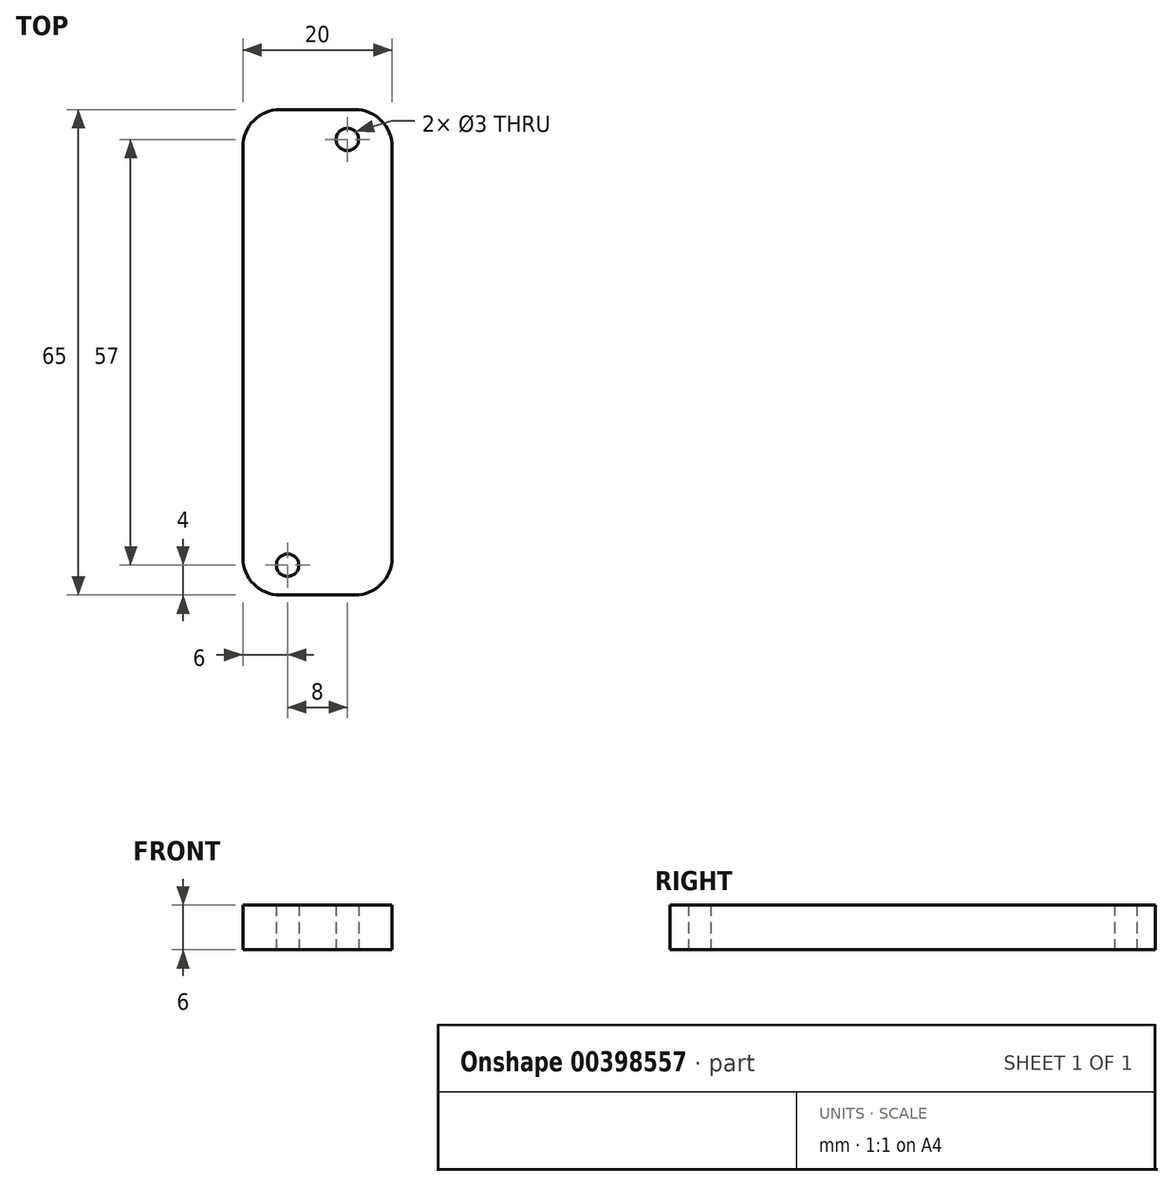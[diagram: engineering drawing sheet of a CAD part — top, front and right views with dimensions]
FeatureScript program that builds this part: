
annotation { "Feature Type Name" : "Feature", "Feature Type Description" : "" }
export const myFeature = defineFeature(function(context is Context, id is Id, definition is map)
    precondition{}
    {
        {
            var Q0;
            Q0=qCreatedBy(makeId("Top.planeOp"),FACE);
            var sketch = newSketch(context, id + "F0", { "sketchPlane" : qUnion([Q0])});
            skLineSegment(sketch, "E0.bottom", {"start": v(10, -32.5) * mm, "end": v(5.75, -32.5) * mm});
            skLineSegment(sketch, "E0.top", {"start": v(10, 32.5) * mm, "end": v(-10, 32.5) * mm});
            skLineSegment(sketch, "E0.left", {"start": v(10, -32.5) * mm, "end": v(10, 32.5) * mm});
            skLineSegment(sketch, "E0.right", {"start": v(-10, -32.5) * mm, "end": v(-10, 32.5) * mm});
            skPoint(sketch, "E1", {"position": v(-4, -28.5) * mm});
            skPoint(sketch, "E2", {"position": v(4, 28.5) * mm});
            skCircle(sketch, "E3", {"center": v(4, 28.5) * mm, "radius": 1.5 * mm});
            skCircle(sketch, "E4", {"center": v(-4, -28.5) * mm, "radius": 1.5 * mm});
            skLineSegment(sketch, "E5.trimOffspring", {"start": v(0.5, -32.5) * mm, "end": v(-10, -32.5) * mm});
            skLineSegment(sketch, "E6", {"start": v(5.75, -32.5) * mm, "end": v(0.5, -32.5) * mm});
            skSolve(sketch);
        }
        {
            var Q0;
            Q0=makeQuery(id+"F0.imprint","IMPRINT",FACE,{"disambiguationData":[TD([[makeQuery(id+"F0.imprint","IMPRINT",EDGE,{"derivedFrom":sQuery(id+"F0.wireOp",EDGE,"E0.bottom")}),-1.0]])]});
            extrude(context, id + "F1", {"entities" : qUnion([Q0]), "depth" : 6 * mm, "offsetDistance" : 25 * mm});
        }
        {
            var Q0;
            Q0=makeQuery(id+"F1.opExtrude","SWEPT_EDGE",EDGE,{"disambiguationData":[OSD([sQuery(id+"F0.wireOp",EDGE,"E0.top"),sQuery(id+"F0.wireOp",EDGE,"E0.right")])]});
            var Q1;
            Q1=makeQuery(id+"F1.opExtrude","SWEPT_EDGE",EDGE,{"disambiguationData":[OSD([sQuery(id+"F0.wireOp",EDGE,"E0.top"),sQuery(id+"F0.wireOp",EDGE,"E0.left")])]});
            var Q2;
            Q2=makeQuery(id+"F1.opExtrude","SWEPT_EDGE",EDGE,{"disambiguationData":[OSD([sQuery(id+"F0.wireOp",EDGE,"E0.bottom"),sQuery(id+"F0.wireOp",EDGE,"E0.left")])]});
            var Q3;
            Q3=makeQuery(id+"F1.opExtrude","SWEPT_EDGE",EDGE,{"disambiguationData":[OSD([sQuery(id+"F0.wireOp",EDGE,"E0.right"),sQuery(id+"F0.wireOp",EDGE,"E5.trimOffspring")])]});
            fillet(context, id + "F2", {"entities" : qUnion([Q0, Q1, Q2, Q3]), "radius" : 5 * mm, "tangentPropagation" : true, "allowEdgeOverflow" : false});
        }
    });
